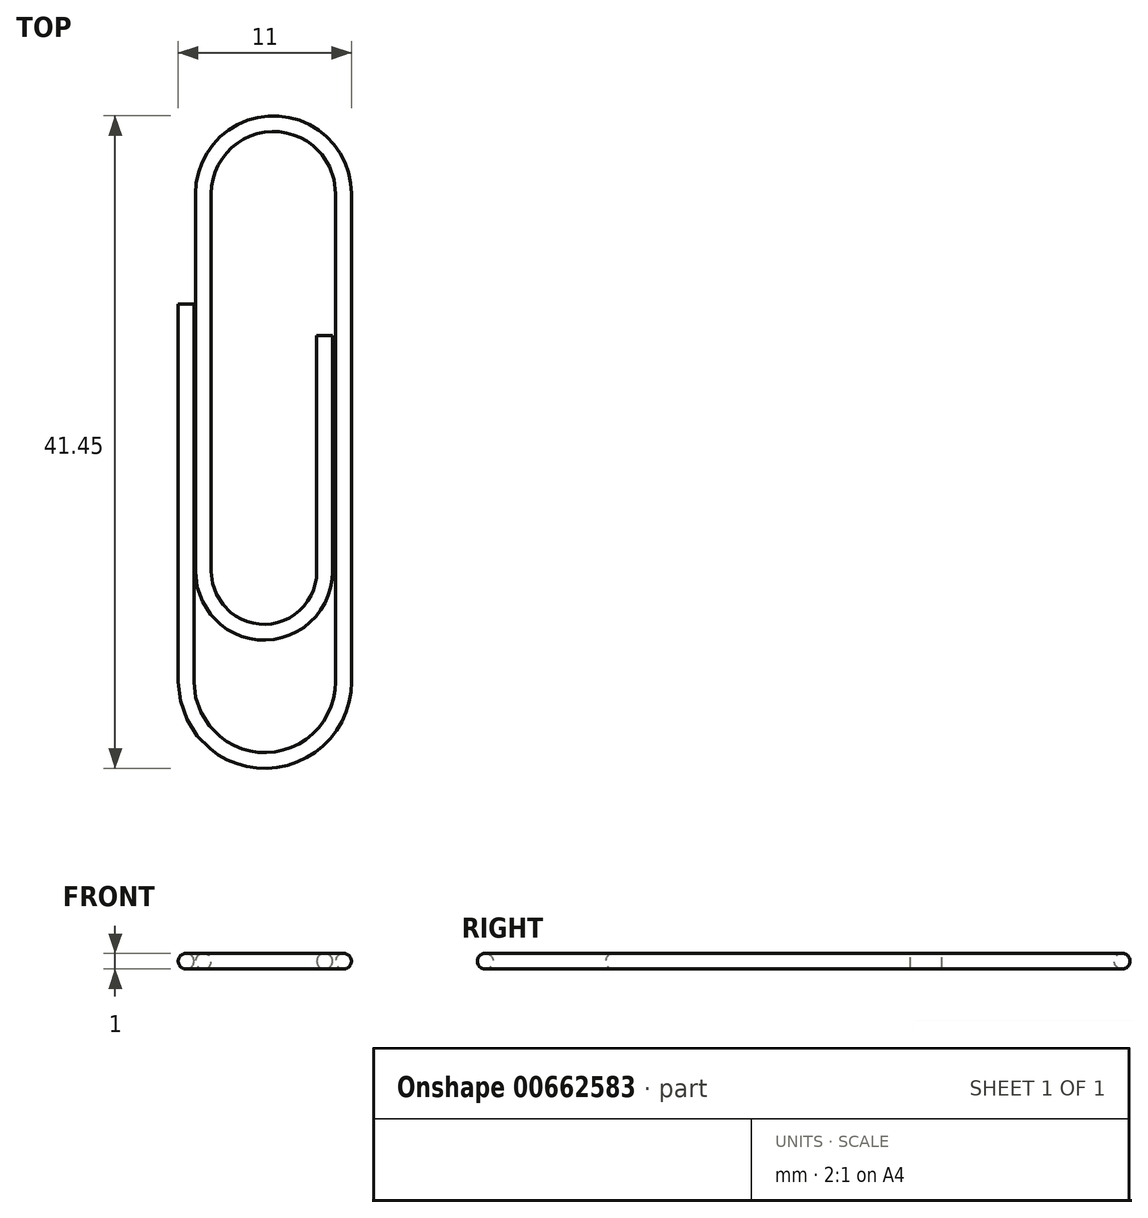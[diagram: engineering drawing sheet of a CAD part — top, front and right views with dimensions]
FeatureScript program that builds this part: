
annotation { "Feature Type Name" : "Feature", "Feature Type Description" : "" }
export const myFeature = defineFeature(function(context is Context, id is Id, definition is map)
    precondition{}
    {
        {
            var Q0;
            Q0=qCreatedBy(makeId("Top.planeOp"),FACE);
            var sketch = newSketch(context, id + "F0", { "sketchPlane" : qUnion([Q0])});
            skLineSegment(sketch, "E0", {"start": v(8.8, -17) * mm, "end": v(8.8, -2) * mm});
            skLineSegment(sketch, "E1", {"start": v(1.1, -17) * mm, "end": v(1.1, 7) * mm});
            skArc(sketch, "E2", {"start": v(1.1, -17) * mm, "mid": v(4.95, -20.85) * mm, "end": v(8.8, -17) * mm});
            skLineSegment(sketch, "E3", {"start": v(10, 7) * mm, "end": v(10, -24) * mm});
            skArc(sketch, "E4", {"start": v(10, 7) * mm, "mid": v(5.55, 11.45) * mm, "end": v(1.1, 7) * mm});
            skLineSegment(sketch, "E5", {"start": v(0, -24) * mm, "end": v(0, 0) * mm});
            skArc(sketch, "E6", {"start": v(0, -24) * mm, "mid": v(5, -29) * mm, "end": v(10, -24) * mm});
            skSolve(sketch);
        }
        {
            var Q0;
            Q0=qCreatedBy(makeId("Front.planeOp"),FACE);
            var sketch = newSketch(context, id + "F1", { "sketchPlane" : qUnion([Q0])});
            skCircle(sketch, "E7", {"center": v(0, 0) * mm, "radius": 0.5 * mm});
            skSolve(sketch);
        }
        {
            var Q0;
            Q0=qSketchRegion(id+"F1",true);
            var Q1;
            Q1=qConstructionFilter(qBodyType(qCreatedBy(id+"F0",EDGE),BodyType.WIRE),ConstructionObject.NO);
            sweep(context, id + "F2", {"profiles" : qUnion([Q0]), "path" : qUnion([Q1])});
        }
    });
